# Revit family: Gira_102200
name_source: partatom
category: Elektroinstallationen
revit_build: Autodesk Revit 2017 (Build: 20160225_1515(x64)
units: mm (PartAtom-declared; Revit-internal decimal feet)

## family parameters
Basisbauteil = Fläche
Beim Laden mit Abzugskörper schneiden = Nein
Bemaßung runder Anschluss = Durchmesser verwenden
Beschriftungsausrichtung beibehalten = Nein
Gemeinsam genutzt = Nein
Raumberechnungspunkt = Nein
Teiletyp = Normal

## types (1)
- Analogaktor 4f KNX REG
    Andere Bussysteme = ohne
    Anzahl der Ausgänge = 4
    Anzahl der binären Eingänge = 0
    Ausführung Text = Basismodul
    Ausgangsspannung [Volt] = [24:24]
    Ausgangsstrom [Ampere] = [0:0,002]
    BIM = https://media.stage.bim.site 8f.rfa
    BIMSITE_PRODUCT_ID = ffad6add8957c80dd5aa2fe34f42ae5410f82fd3
    Beschreibung = KNX Analogaktor 4fach  REG plus Merkmale:  Analogaktor 4fach REG mit integrierter Busankopplung wandelt KNX Telegramme (1-Byte und 2-Byte) in analoge Ausgangssignale um.  Diese analogen Ausgangssignale ermöglichen es Aktoren der Heizungs-, Klima- und Lüftungstechnik ihre Ausgangsgrößen aufgrund von Businformationen anzupassen und an Regelprozessen teilzunehmen.  Spannungsausgänge mit Kurzschlussüberwachung.  Der Ausgangszustand wird durch die Status-LED angezeigt.  Die Ausgangsgrößen können zwangsgeführt werden.  Nicht benötigte Ausgänge lassen sich abschalten.  Die vier Ausgänge werden durch die Software auf Spannungs- oder Stromsignale parametriert.
    Breite in Teilungseinheiten = 4
    Bussystem Funkbus = Nein
    Bussystem KNX = Ja
    Bussystem KNX-Funk = Nein
    Bussystem LON = Ja
    Bussystem Powernet = Nein
    Datenblatt = https://media.stage.bim.site
    Datenblatt 1 = https://media.stage.bim.site
    GTIN = 4010337010708
    Geeignet für C-Last = Nein
    HAN = 102200
    HeinzeBIM = https://www.heinze.de
    Hersteller = Gira
    Kosten = 0 $
    Max. Anzahl der Schaltausgänge = 0
    Mit Busankopplung = Ja
    Mit LED-Anzeige = Nein
    Montageart = REG
    Produktseite = https://media.stage.bim.site
    Schutzart (IP) = IP20
    Typname = Analogaktor 4f KNX REG
    URL = https://www.gira.de
    Vor Ort-/Handbedienung = Nein
    Vorgabe-Ansicht = 1219 mm

## geometry (parser evidence)
native form markers: Sweep x2
no freeform markers — native parametric forms only
